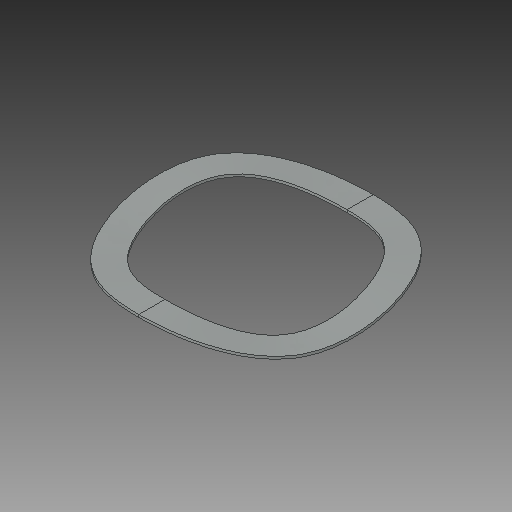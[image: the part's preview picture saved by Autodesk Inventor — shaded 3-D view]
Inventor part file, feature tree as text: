
AUTODESK INVENTOR PART (.ipt)
format: ipt  version: 2017 (Build 210142000, 142)  size: 123,904 bytes
history: native  units: in
note: dims shown in document units (in); Inventor stores cm internally (conversion verified against a paired STEP export)
features: loft x1
ambient origin geometry x8: Origin, YZ Plane, XZ Plane, XY Plane, X Axis, Y Axis, Z Axis, Center Point
bodies: Solid1 (feature_tree)
feature tree (1):
  loft  "Loft1"
